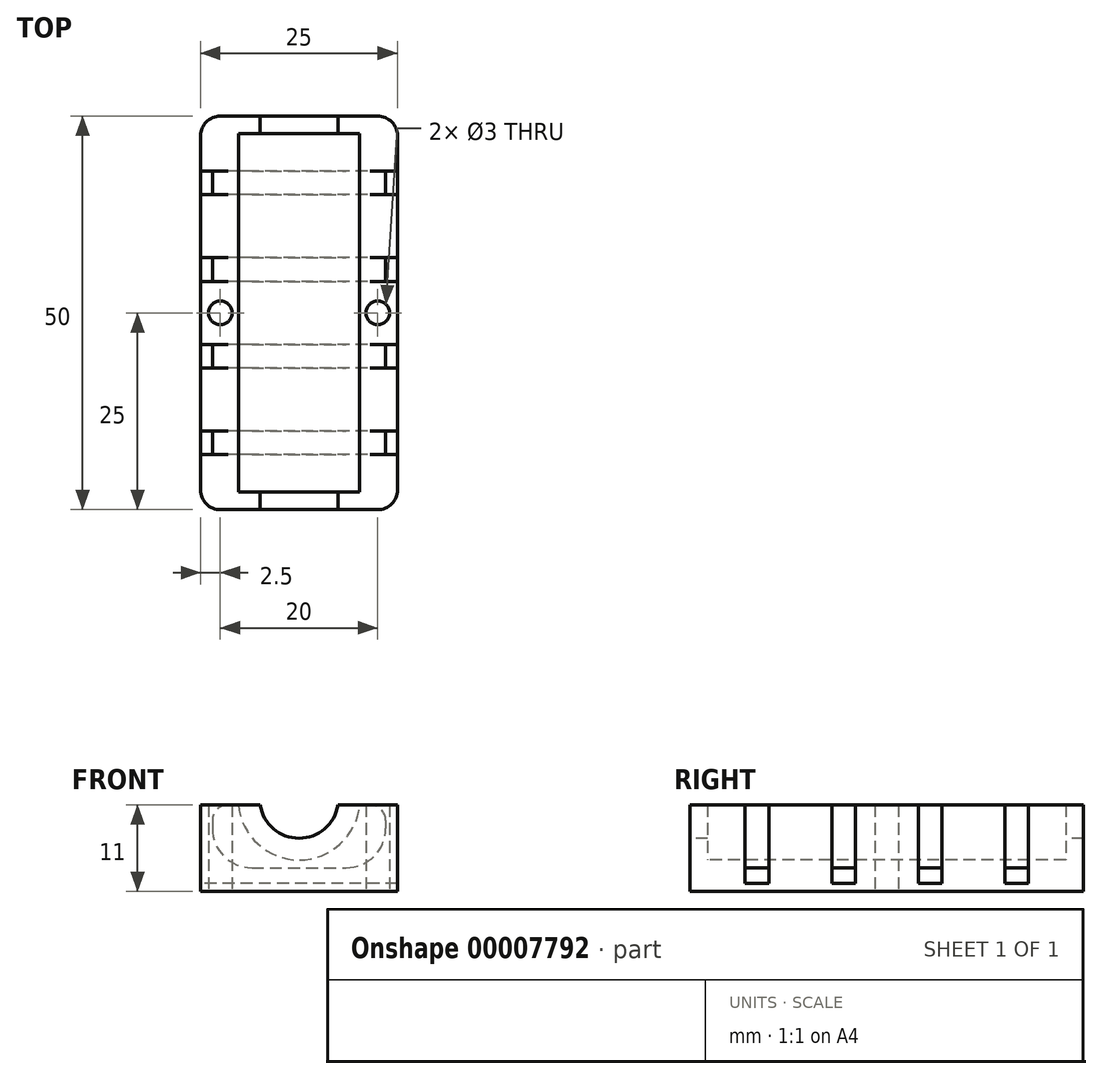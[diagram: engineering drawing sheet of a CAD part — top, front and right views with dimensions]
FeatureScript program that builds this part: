
annotation { "Feature Type Name" : "Feature", "Feature Type Description" : "" }
export const myFeature = defineFeature(function(context is Context, id is Id, definition is map)
    precondition{}
    {
        {
            var Q0;
            Q0=qCreatedBy(makeId("Front.planeOp"),FACE);
            var sketch = newSketch(context, id + "F0", { "sketchPlane" : qUnion([Q0])});
            skCircle(sketch, "E0", {"center": v(0, 11.75) * mm, "radius": 7.75 * mm, "construction": true});
            skLineSegment(sketch, "E1", {"start": v(-23.37, 11) * mm, "end": v(23.37, 11) * mm, "construction": true});
            skSolve(sketch);
        }
        {
            var Q0;
            Q0=qCreatedBy(makeId("Front.planeOp"),FACE);
            var sketch = newSketch(context, id + "F1", { "sketchPlane" : qUnion([Q0])});
            skLineSegment(sketch, "E2.bottom", {"start": v(-12.5, 11) * mm, "end": v(12.5, 11) * mm});
            skLineSegment(sketch, "E2.top", {"start": v(-12.5, 0) * mm, "end": v(12.5, 0) * mm});
            skLineSegment(sketch, "E2.left", {"start": v(-12.5, 11) * mm, "end": v(-12.5, 0) * mm});
            skLineSegment(sketch, "E2.right", {"start": v(12.5, 11) * mm, "end": v(12.5, 0) * mm});
            skSolve(sketch);
        }
        {
            var Q0;
            Q0=makeQuery(id+"F1.imprint","IMPRINT",FACE,{"disambiguationData":[TD([[makeQuery(id+"F1.imprint","IMPRINT",EDGE,{"derivedFrom":sQuery(id+"F1.wireOp",EDGE,"E2.bottom")}),-1.0]])]});
            extrude(context, id + "F2", {"entities" : qUnion([Q0]), "endBound" : BoundingType.SYMMETRIC, "depth" : 50 * mm});
        }
        {
            var Q0;
            Q0=qCreatedBy(makeId("Top.planeOp"),FACE);
            var sketch = newSketch(context, id + "F3", { "sketchPlane" : qUnion([Q0])});
            skLineSegment(sketch, "E3.bottom", {"start": v(-25, 18) * mm, "end": v(25, 18) * mm});
            skLineSegment(sketch, "E3.top", {"start": v(-25, 15) * mm, "end": v(25, 15) * mm});
            skLineSegment(sketch, "E3.left", {"start": v(-25, 18) * mm, "end": v(-25, 15) * mm});
            skLineSegment(sketch, "E3.right", {"start": v(25, 18) * mm, "end": v(25, 15) * mm});
            skLineSegment(sketch, "E4.bottom", {"start": v(-25, 7) * mm, "end": v(25, 7) * mm});
            skLineSegment(sketch, "E4.top", {"start": v(-25, 4) * mm, "end": v(25, 4) * mm});
            skLineSegment(sketch, "E4.left", {"start": v(-25, 7) * mm, "end": v(-25, 4) * mm});
            skLineSegment(sketch, "E4.right", {"start": v(25, 7) * mm, "end": v(25, 4) * mm});
            skLineSegment(sketch, "E5.bottom", {"start": v(-25, -4) * mm, "end": v(25, -4) * mm});
            skLineSegment(sketch, "E5.top", {"start": v(-25, -7) * mm, "end": v(25, -7) * mm});
            skLineSegment(sketch, "E5.left", {"start": v(-25, -4) * mm, "end": v(-25, -7) * mm});
            skLineSegment(sketch, "E5.right", {"start": v(25, -4) * mm, "end": v(25, -7) * mm});
            skLineSegment(sketch, "E6.bottom", {"start": v(-25, -15) * mm, "end": v(25, -15) * mm});
            skLineSegment(sketch, "E6.top", {"start": v(-25, -18) * mm, "end": v(25, -18) * mm});
            skLineSegment(sketch, "E6.left", {"start": v(-25, -15) * mm, "end": v(-25, -18) * mm});
            skLineSegment(sketch, "E6.right", {"start": v(25, -15) * mm, "end": v(25, -18) * mm});
            skSolve(sketch);
        }
        {
            var Q0;
            Q0=makeQuery(id+"F3.imprint","IMPRINT",FACE,{"disambiguationData":[TD([[makeQuery(id+"F3.imprint","IMPRINT",EDGE,{"derivedFrom":sQuery(id+"F3.wireOp",EDGE,"E3.bottom")}),-1.0]])]});
            var Q1;
            Q1=makeQuery(id+"F3.imprint","IMPRINT",FACE,{"disambiguationData":[TD([[makeQuery(id+"F3.imprint","IMPRINT",EDGE,{"derivedFrom":sQuery(id+"F3.wireOp",EDGE,"E4.bottom")}),-1.0]])]});
            var Q2;
            Q2=makeQuery(id+"F3.imprint","IMPRINT",FACE,{"disambiguationData":[TD([[makeQuery(id+"F3.imprint","IMPRINT",EDGE,{"derivedFrom":sQuery(id+"F3.wireOp",EDGE,"E5.bottom")}),-1.0]])]});
            var Q3;
            Q3=makeQuery(id+"F3.imprint","IMPRINT",FACE,{"disambiguationData":[TD([[makeQuery(id+"F3.imprint","IMPRINT",EDGE,{"derivedFrom":sQuery(id+"F3.wireOp",EDGE,"E6.bottom")}),-1.0]])]});
            extrude(context, id + "F4", {"entities" : qUnion([Q0, Q1, Q2, Q3]), "operationType" : NewBodyOperationType.REMOVE, "endBound" : BoundingType.UP_TO_NEXT, "depth" : 25 * mm});
        }
        {
            var Q0;
            Q0=qCreatedBy(makeId("Front.planeOp"),FACE);
            var sketch = newSketch(context, id + "F5", { "sketchPlane" : qUnion([Q0])});
            skLineSegment(sketch, "E7.bottom", {"start": v(-9, 11) * mm, "end": v(9, 11) * mm});
            skLineSegment(sketch, "E7.top", {"start": v(-6, 3) * mm, "end": v(6, 3) * mm});
            skLineSegment(sketch, "E7.left", {"start": v(-11, 9) * mm, "end": v(-11, 8) * mm});
            skLineSegment(sketch, "E7.right", {"start": v(11, 9) * mm, "end": v(11, 8) * mm});
            skPoint(sketch, "E8.visualSharp", {"position": v(-11, 3) * mm});
            skArc(sketch, "E8.filletArc", {"start": v(-11, 8) * mm, "mid": v(-9.54, 4.46) * mm, "end": v(-6, 3) * mm});
            skPoint(sketch, "E9.visualSharp", {"position": v(11, 3) * mm});
            skArc(sketch, "E9.filletArc", {"start": v(6, 3) * mm, "mid": v(9.54, 4.46) * mm, "end": v(11, 8) * mm});
            skPoint(sketch, "E10.visualSharp", {"position": v(-11, 11) * mm});
            skArc(sketch, "E10.filletArc", {"start": v(-9, 11) * mm, "mid": v(-10.41, 10.41) * mm, "end": v(-11, 9) * mm});
            skPoint(sketch, "E11.visualSharp", {"position": v(11, 11) * mm});
            skArc(sketch, "E11.filletArc", {"start": v(11, 9) * mm, "mid": v(10.41, 10.41) * mm, "end": v(9, 11) * mm});
            skSolve(sketch);
        }
        {
            var Q0;
            Q0 = qSketchRegion(id + "F5", true);
            extrude(context, id + "F6", {"entities" : qUnion([Q0]), "operationType" : NewBodyOperationType.ADD, "endBound" : BoundingType.SYMMETRIC, "depth" : 45 * mm});
        }
        {
            var Q0;
            Q0=qCreatedBy(makeId("Front.planeOp"),FACE);
            var sketch = newSketch(context, id + "F7", { "sketchPlane" : qUnion([Q0])});
            skCircle(sketch, "E12", {"center": v(0, 11.75) * mm, "radius": 7.75 * mm});
            skSolve(sketch);
        }
        {
            var Q0;
            Q0 = qSketchRegion(id + "F7", true);
            extrude(context, id + "F8", {"entities" : qUnion([Q0]), "operationType" : NewBodyOperationType.REMOVE, "endBound" : BoundingType.SYMMETRIC, "oppositeDirection" : true, "depth" : 45.5 * mm});
        }
        {
            var Q0;
            Q0=qCreatedBy(makeId("Front.planeOp"),FACE);
            var sketch = newSketch(context, id + "F9", { "sketchPlane" : qUnion([Q0])});
            skLineSegment(sketch, "E13.bottom", {"start": v(12.5, 1) * mm, "end": v(-12.5, 1) * mm});
            skLineSegment(sketch, "E13.top", {"start": v(12.5, 0) * mm, "end": v(-12.5, 0) * mm});
            skLineSegment(sketch, "E13.left", {"start": v(12.5, 1) * mm, "end": v(12.5, 0) * mm});
            skLineSegment(sketch, "E13.right", {"start": v(-12.5, 1) * mm, "end": v(-12.5, 0) * mm});
            skSolve(sketch);
        }
        {
            var Q0;
            Q0 = qSketchRegion(id + "F9", true);
            extrude(context, id + "F10", {"entities" : qUnion([Q0]), "operationType" : NewBodyOperationType.ADD, "endBound" : BoundingType.SYMMETRIC, "depth" : 50 * mm});
        }
        {
            var Q0;
            Q0=qCreatedBy(makeId("Front.planeOp"),FACE);
            var sketch = newSketch(context, id + "F11", { "sketchPlane" : qUnion([Q0])});
            skCircle(sketch, "E14", {"center": v(0, 11.75) * mm, "radius": 5 * mm});
            skSolve(sketch);
        }
        {
            var Q0;
            Q0 = qSketchRegion(id + "F11", true);
            extrude(context, id + "F12", {"entities" : qUnion([Q0]), "operationType" : NewBodyOperationType.REMOVE, "endBound" : BoundingType.SYMMETRIC, "oppositeDirection" : true, "depth" : 65.12 * mm});
        }
        {
            var Q0;
            Q0=makeQuery(id+"F2.opExtrude","CAP_EDGE",EDGE,{"disambiguationData":[OSD([sQuery(id+"F1.wireOp",EDGE,"E2.right")])],"isStart":false});
            var Q1;
            Q1=makeQuery(id+"F2.opExtrude","CAP_EDGE",EDGE,{"disambiguationData":[OSD([sQuery(id+"F1.wireOp",EDGE,"E2.left")])],"isStart":false});
            var Q2;
            Q2=makeQuery(id+"F2.opExtrude","CAP_EDGE",EDGE,{"disambiguationData":[OSD([sQuery(id+"F1.wireOp",EDGE,"E2.left")])],"isStart":true});
            var Q3;
            Q3=makeQuery(id+"F2.opExtrude","CAP_EDGE",EDGE,{"disambiguationData":[OSD([sQuery(id+"F1.wireOp",EDGE,"E2.right")])],"isStart":true});
            fillet(context, id + "F13", {"entities" : qUnion([Q0, Q1, Q2, Q3]), "radius" : 2.5 * mm, "tangentPropagation" : true, "allowEdgeOverflow" : false});
        }
        {
            var Q0;
            Q0=qCreatedBy(makeId("Top.planeOp"),FACE);
            var sketch = newSketch(context, id + "F14", { "sketchPlane" : qUnion([Q0])});
            skCircle(sketch, "E15", {"center": v(-10, 0) * mm, "radius": 1.5 * mm});
            skCircle(sketch, "E16", {"center": v(10, 0) * mm, "radius": 1.5 * mm});
            skSolve(sketch);
        }
        {
            var Q0;
            Q0 = qSketchRegion(id + "F14", true);
            extrude(context, id + "F15", {"entities" : qUnion([Q0]), "operationType" : NewBodyOperationType.REMOVE, "endBound" : BoundingType.THROUGH_ALL, "depth" : 25 * mm});
        }
    });
